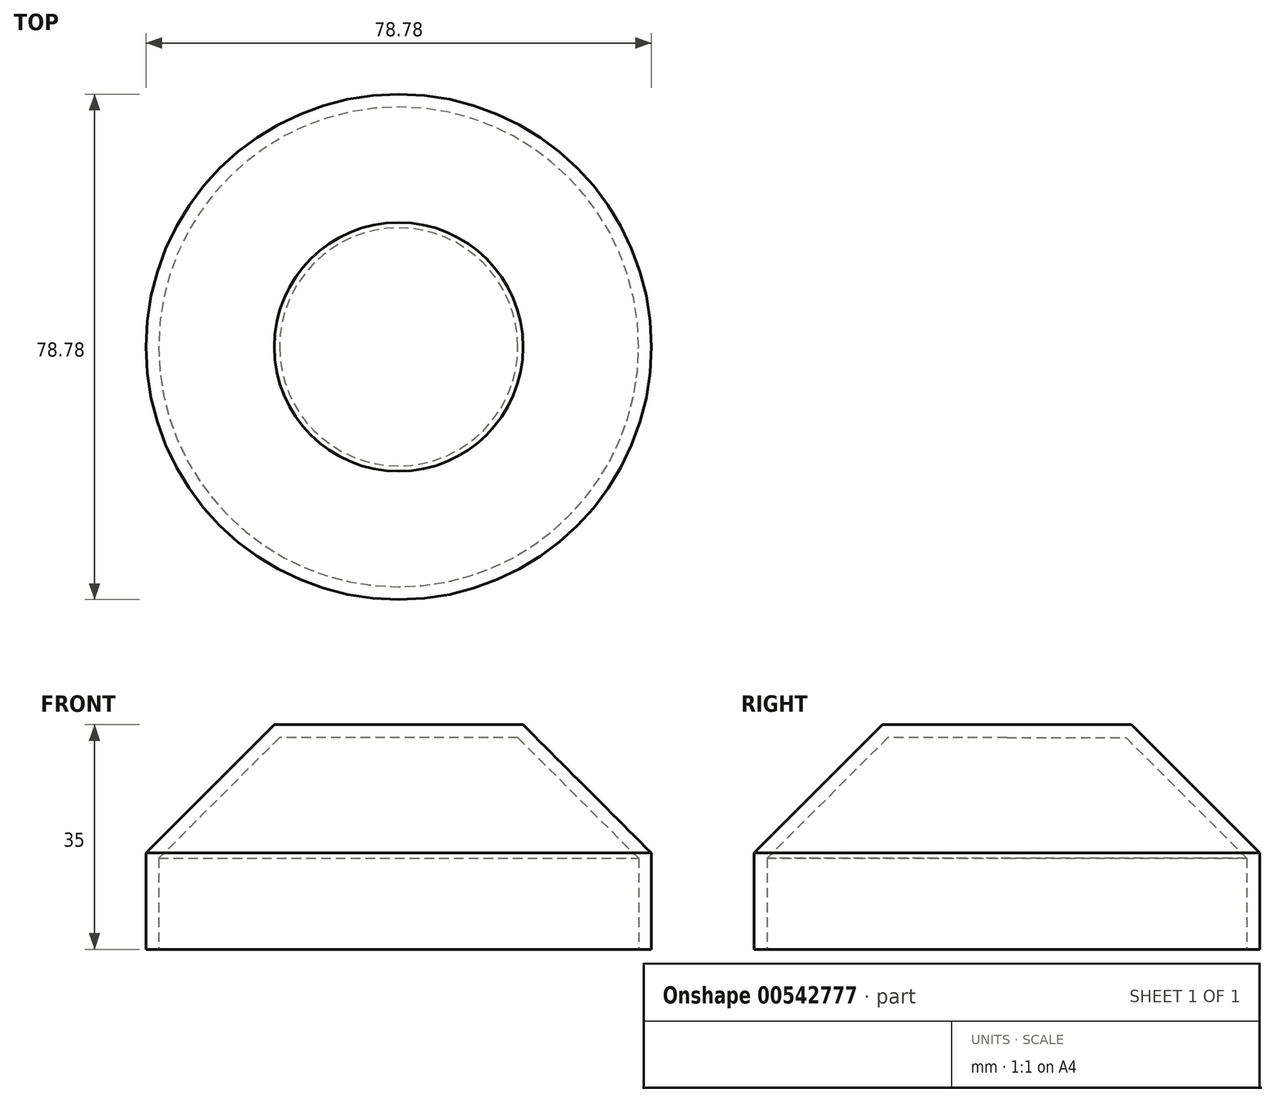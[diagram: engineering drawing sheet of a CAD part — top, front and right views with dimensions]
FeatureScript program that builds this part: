
annotation { "Feature Type Name" : "Feature", "Feature Type Description" : "" }
export const myFeature = defineFeature(function(context is Context, id is Id, definition is map)
    precondition{}
    {
        {
            var Q0;
            Q0=qCreatedBy(makeId("Top.planeOp"),FACE);
            var sketch = newSketch(context, id + "F0", { "sketchPlane" : qUnion([Q0])});
            skCircle(sketch, "E0", {"center": v(0, 0) * mm, "radius": 39.39 * mm});
            skSolve(sketch);
        }
        {
            var Q0;
            Q0=makeQuery(id+"F0.imprint","IMPRINT",FACE,{"disambiguationData":[TD([[makeQuery(id+"F0.imprint","IMPRINT",EDGE,{"derivedFrom":sQuery(id+"F0.wireOp",EDGE,"E0")}),1.0]])]});
            var Q1;
            Q1=sQuery(id+"F0.wireOp",EDGE,"E0");
            extrude(context, id + "F1", {"entities" : qUnion([Q0]), "surfaceEntities" : qUnion([Q1]), "depth" : 25 * mm, "offsetDistance" : 25 * mm, "hasSecondDirection" : true, "secondDirectionOppositeDirection" : true, "secondDirectionDepth" : 10 * mm});
        }
        {
            var Q0;
            Q0=makeQuery(id+"F1.opExtrude","CAP_FACE",FACE,{"disambiguationData":[OSD([sQuery(id+"F0.wireOp",EDGE,"E0")])],"isStart":false});
            chamfer(context, id + "F2", {"entities" : qUnion([Q0]), "width" : 20 * mm, "tangentPropagation" : true});
        }
        {
            var Q0;
            Q0=makeQuery(id+"F1.opExtrude","CAP_FACE",FACE,{"disambiguationData":[OSD([sQuery(id+"F0.wireOp",EDGE,"E0")])],"isStart":true});
            shell(context, id + "F3", {"entities" : qUnion([Q0]), "thickness" : 2 * mm});
        }
    });
